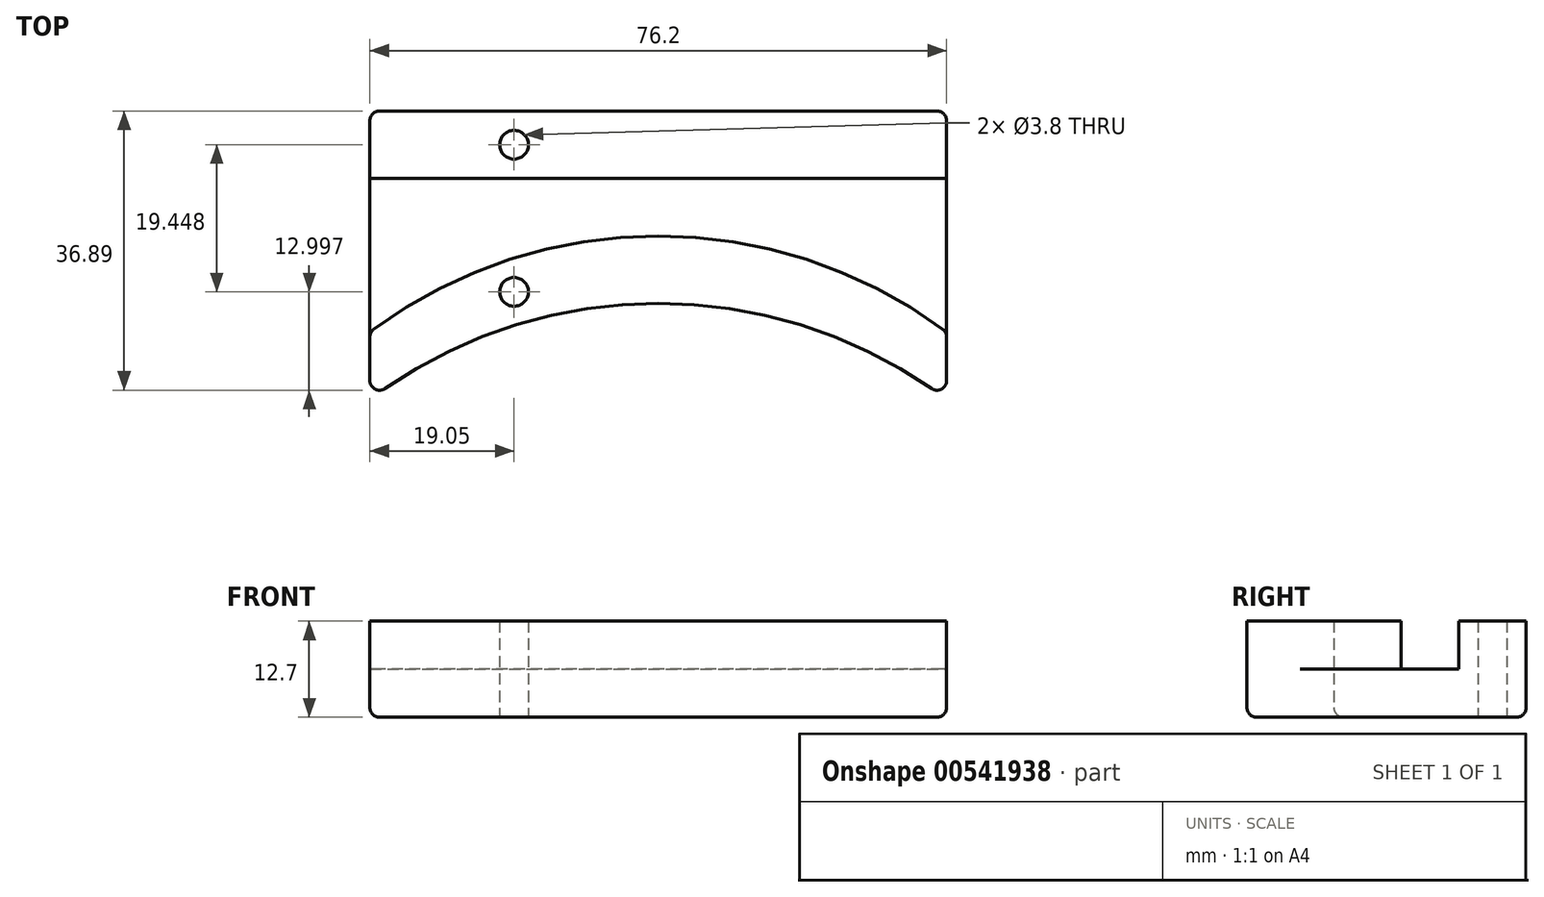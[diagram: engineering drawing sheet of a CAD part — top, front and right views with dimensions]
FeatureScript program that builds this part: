
annotation { "Feature Type Name" : "Feature", "Feature Type Description" : "" }
export const myFeature = defineFeature(function(context is Context, id is Id, definition is map)
    precondition{}
    {
        {
            var Q0;
            Q0=qCreatedBy(makeId("Top.planeOp"),FACE);
            var sketch = newSketch(context, id + "F0", { "sketchPlane" : qUnion([Q0])});
            skLineSegment(sketch, "E0", {"start": v(-38.1, 0) * mm, "end": v(38.1, 0) * mm});
            skLineSegment(sketch, "E1", {"start": v(38.1, 0) * mm, "end": v(38.1, -38.1) * mm});
            skArc(sketch, "E2", {"start": v(38.1, -38.1) * mm, "mid": v(0, -25.4) * mm, "end": v(-38.1, -38.1) * mm});
            skLineSegment(sketch, "E3", {"start": v(-38.1, 0) * mm, "end": v(-38.1, -38.1) * mm});
            skSolve(sketch);
        }
        {
            var Q0;
            Q0 = qSketchRegion(id + "F0", true);
            extrude(context, id + "F1", {"entities" : qUnion([Q0]), "depth" : 6.35 * mm, "offsetDistance" : 25.4 * mm});
        }
        {
            var Q0;
            Q0=makeQuery(id+"F1.opExtrude","CAP_FACE",FACE,{"disambiguationData":[OSD([sQuery(id+"F0.wireOp",EDGE,"E0"),sQuery(id+"F0.wireOp",EDGE,"E1"),sQuery(id+"F0.wireOp",EDGE,"E2"),sQuery(id+"F0.wireOp",EDGE,"E3")])],"isStart":false});
            var sketch = newSketch(context, id + "F2", { "sketchPlane" : qUnion([Q0])});
            skLineSegment(sketch, "E4.bottom", {"start": v(-38.1, 0) * mm, "end": v(38.1, 0) * mm});
            skLineSegment(sketch, "E4.top", {"start": v(-38.1, -8.89) * mm, "end": v(38.1, -8.89) * mm});
            skLineSegment(sketch, "E4.left", {"start": v(-38.1, 0) * mm, "end": v(-38.1, -8.89) * mm});
            skLineSegment(sketch, "E4.right", {"start": v(38.1, 0) * mm, "end": v(38.1, -8.89) * mm});
            skLineSegment(sketch, "E5", {"start": v(-38.1, -38.1) * mm, "end": v(-38.1, -29.21) * mm});
            skLineSegment(sketch, "E6", {"start": v(38.1, -38.1) * mm, "end": v(38.1, -29.21) * mm});
            skArc(sketch, "E7", {"start": v(38.1, -29.21) * mm, "mid": v(0, -16.51) * mm, "end": v(-38.1, -29.21) * mm});
            skArc(sketch, "E8", {"start": v(38.1, -38.1) * mm, "mid": v(0, -25.4) * mm, "end": v(-38.1, -38.1) * mm});
            skSolve(sketch);
        }
        {
            var Q0;
            Q0 = qSketchRegion(id + "F2", true);
            extrude(context, id + "F3", {"entities" : qUnion([Q0]), "operationType" : NewBodyOperationType.ADD, "depth" : 6.35 * mm, "offsetDistance" : 25.4 * mm});
        }
        {
            var Q0;
            Q0=makeQuery(id+"F3.opExtrude","CAP_FACE",FACE,{"disambiguationData":[OSD([sQuery(id+"F2.wireOp",EDGE,"E4.bottom"),sQuery(id+"F2.wireOp",EDGE,"E4.top"),sQuery(id+"F2.wireOp",EDGE,"E4.left"),sQuery(id+"F2.wireOp",EDGE,"E4.right")])],"isStart":false});
            var sketch = newSketch(context, id + "F4", { "sketchPlane" : qUnion([Q0])});
            skLineSegment(sketch, "E9", {"start": v(-19.05, -4.44) * mm, "end": v(-19.05, -23.9) * mm, "construction": true});
            skLineSegment(sketch, "E10", {"start": v(19.05, -23.9) * mm, "end": v(-19.05, -23.9) * mm, "construction": true});
            skLineSegment(sketch, "E11", {"start": v(-19.05, -4.44) * mm, "end": v(19.05, -4.44) * mm, "construction": true});
            skLineSegment(sketch, "E12", {"start": v(19.05, -4.44) * mm, "end": v(19.05, -23.9) * mm, "construction": true});
            skLineSegment(sketch, "E13", {"start": v(-20.24, -19.82) * mm, "end": v(-19.05, -23.9) * mm, "construction": true});
            skLineSegment(sketch, "E14", {"start": v(-17.86, -27.96) * mm, "end": v(-19.05, -23.9) * mm, "construction": true});
            skLineSegment(sketch, "E15", {"start": v(20.24, -19.82) * mm, "end": v(19.05, -23.9) * mm, "construction": true});
            skLineSegment(sketch, "E16", {"start": v(19.05, -23.9) * mm, "end": v(17.86, -27.96) * mm, "construction": true});
            skLineSegment(sketch, "E17", {"start": v(-17.86, -27.96) * mm, "end": v(-3.14, -23.65) * mm, "construction": true});
            skLineSegment(sketch, "E18", {"start": v(-12.06, -4.44) * mm, "end": v(-12.06, 0) * mm, "construction": true});
            skLineSegment(sketch, "E19", {"start": v(-12.06, -4.44) * mm, "end": v(-12.06, -8.89) * mm, "construction": true});
            skSolve(sketch);
        }
        {
            var Q0;
            Q0=makeQuery(id+"F3.boolean.opBoolean","MERGE",EDGE,{"derivedFrom":[makeQuery(id+"F1.opExtrude","SWEPT_EDGE",EDGE,{"disambiguationData":[OSD([sQuery(id+"F0.wireOp",EDGE,"E0"),sQuery(id+"F0.wireOp",EDGE,"E3")])]}),makeQuery(id+"F3.opExtrude","SWEPT_EDGE",EDGE,{"disambiguationData":[OSD([sQuery(id+"F2.wireOp",EDGE,"E4.bottom"),sQuery(id+"F2.wireOp",EDGE,"E4.left")])]})]});
            var Q1;
            Q1=makeQuery(id+"F1.opExtrude","CAP_EDGE",EDGE,{"disambiguationData":[OSD([sQuery(id+"F0.wireOp",EDGE,"E3")])],"isStart":true});
            var Q2;
            Q2=makeQuery(id+"F3.boolean.opBoolean","MERGE",EDGE,{"derivedFrom":[makeQuery(id+"F1.opExtrude","SWEPT_EDGE",EDGE,{"disambiguationData":[OSD([sQuery(id+"F0.wireOp",EDGE,"E2"),sQuery(id+"F0.wireOp",EDGE,"E3")])]}),makeQuery(id+"F3.opExtrude","SWEPT_EDGE",EDGE,{"disambiguationData":[OSD([sQuery(id+"F2.wireOp",EDGE,"E5"),sQuery(id+"F2.wireOp",EDGE,"E8")])]})]});
            var Q3;
            Q3=makeQuery(id+"F3.boolean.opBoolean","MERGE",EDGE,{"derivedFrom":[makeQuery(id+"F1.opExtrude","SWEPT_EDGE",EDGE,{"disambiguationData":[OSD([sQuery(id+"F0.wireOp",EDGE,"E1"),sQuery(id+"F0.wireOp",EDGE,"E2")])]}),makeQuery(id+"F3.opExtrude","SWEPT_EDGE",EDGE,{"disambiguationData":[OSD([sQuery(id+"F2.wireOp",EDGE,"E6"),sQuery(id+"F2.wireOp",EDGE,"E8")])]})]});
            var Q4;
            Q4=makeQuery(id+"F1.opExtrude","CAP_EDGE",EDGE,{"disambiguationData":[OSD([sQuery(id+"F0.wireOp",EDGE,"E2")])],"isStart":true});
            var Q5;
            Q5=makeQuery(id+"F1.opExtrude","CAP_EDGE",EDGE,{"disambiguationData":[OSD([sQuery(id+"F0.wireOp",EDGE,"E0")])],"isStart":true});
            var Q6;
            Q6=makeQuery(id+"F1.opExtrude","CAP_EDGE",EDGE,{"disambiguationData":[OSD([sQuery(id+"F0.wireOp",EDGE,"E1")])],"isStart":true});
            var Q7;
            Q7=makeQuery(id+"F3.boolean.opBoolean","MERGE",EDGE,{"derivedFrom":[makeQuery(id+"F1.opExtrude","SWEPT_EDGE",EDGE,{"disambiguationData":[OSD([sQuery(id+"F0.wireOp",EDGE,"E0"),sQuery(id+"F0.wireOp",EDGE,"E1")])]}),makeQuery(id+"F3.opExtrude","SWEPT_EDGE",EDGE,{"disambiguationData":[OSD([sQuery(id+"F2.wireOp",EDGE,"E4.bottom"),sQuery(id+"F2.wireOp",EDGE,"E4.right")])]})]});
            var Q8;
            Q8=makeQuery(id+"F3.opExtrude","CAP_EDGE",EDGE,{"disambiguationData":[OSD([sQuery(id+"F2.wireOp",EDGE,"E4.top")])],"isStart":true});
            var Q9;
            Q9=makeQuery(id+"F3.opExtrude","CAP_EDGE",EDGE,{"disambiguationData":[OSD([sQuery(id+"F2.wireOp",EDGE,"E7")])],"isStart":true});
            var Q10;
            Q10=makeQuery(id+"F3.opExtrude","SWEPT_EDGE",EDGE,{"disambiguationData":[OSD([sQuery(id+"F0.wireOp",EDGE,"E3"),sQuery(id+"F2.wireOp",EDGE,"E5"),sQuery(id+"F2.wireOp",EDGE,"E7")])]});
            var Q11;
            Q11=makeQuery(id+"F3.opExtrude","SWEPT_EDGE",EDGE,{"disambiguationData":[OSD([sQuery(id+"F0.wireOp",EDGE,"E1"),sQuery(id+"F2.wireOp",EDGE,"E6"),sQuery(id+"F2.wireOp",EDGE,"E7")])]});
            fillet(context, id + "F5", {"entities" : qUnion([Q0, Q1, Q2, Q3, Q4, Q5, Q6, Q7, Q8, Q9, Q10, Q11]), "radius" : 1.27 * mm, "tangentPropagation" : true, "allowEdgeOverflow" : false});
        }
        {
            var Q0;
            Q0=makeQuery(id+"F1.opExtrude","CAP_FACE",FACE,{"disambiguationData":[OSD([sQuery(id+"F0.wireOp",EDGE,"E0"),sQuery(id+"F0.wireOp",EDGE,"E1"),sQuery(id+"F0.wireOp",EDGE,"E2"),sQuery(id+"F0.wireOp",EDGE,"E3")])],"isStart":true});
            var sketch = newSketch(context, id + "F6", { "sketchPlane" : qUnion([Q0])});
            skPoint(sketch, "E20", {"position": v(-19.05, 4.44) * mm});
            skPoint(sketch, "E21", {"position": v(-19.05, 23.9) * mm});
            skSolve(sketch);
        }
        {
            var Q0;
            Q0=sQuery(id+"F6.wireOp",VERTEX,"E20");
            var Q1;
            Q1=sQuery(id+"F6.wireOp",VERTEX,"E21");
            var Q2;
            Q2=makeQuery(id+"F1.opExtrude","SWEPT_BODY",BODY,{"disambiguationData":[OSD([sQuery(id+"F0.wireOp",EDGE,"E0"),sQuery(id+"F0.wireOp",EDGE,"E1"),sQuery(id+"F0.wireOp",EDGE,"E2"),sQuery(id+"F0.wireOp",EDGE,"E3")])]});
            hole(context, id + "F7", {"style" : HoleStyle.SIMPLE, "endStyle" : HoleEndStyle.THROUGH, "standardTappedOrClearance" : lookupTablePath({ "standard" : "ANSI", "fit" : "Normal (ASME)", "size" : "#6", "type" : "Clearance" }), "standardBlindInLast" : lookupTablePath({ "fit" : "Free", "standard" : "ANSI", "size" : "#6", "type" : "Clearance" }), "holeDiameter" : 3.8 * mm, "isTappedThrough" : true, "tappedDepth" : 12.7 * mm, "tapClearance" : 3, "locations" : qUnion([Q0, Q1]), "scope" : qUnion([Q2])});
        }
    });
